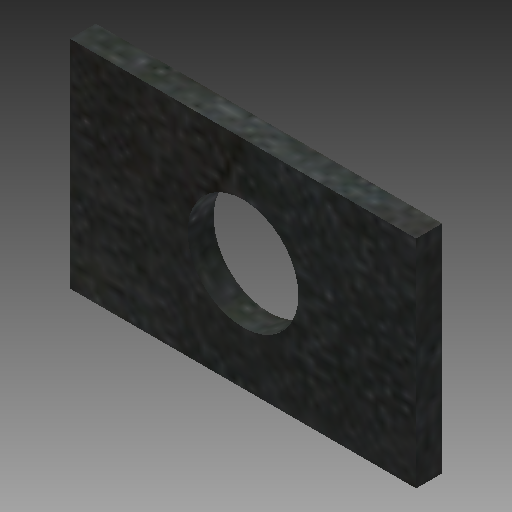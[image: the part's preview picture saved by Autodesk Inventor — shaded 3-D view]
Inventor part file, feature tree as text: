
AUTODESK INVENTOR PART (.ipt)
format: ipt  version: 2019 (Build 230136000, 136)  size: 196,096 bytes
history: native  units: mm
features: extrude x1, sketch x1
ambient origin geometry x8: Origin, YZ Plane, XZ Plane, XY Plane, X Axis, Y Axis, Z Axis, Center Point
bodies: Solid1 (feature_tree)
feature tree (2):
  extrude  "Extrusion1"  Depth=3.0mm
  sketch  "Sketch1"  dims[d0=12.8mm d1=20.0mm d2=40.0mm d3=25.0mm d4=12.5mm d5=3.0mm d6=0.0mm]
